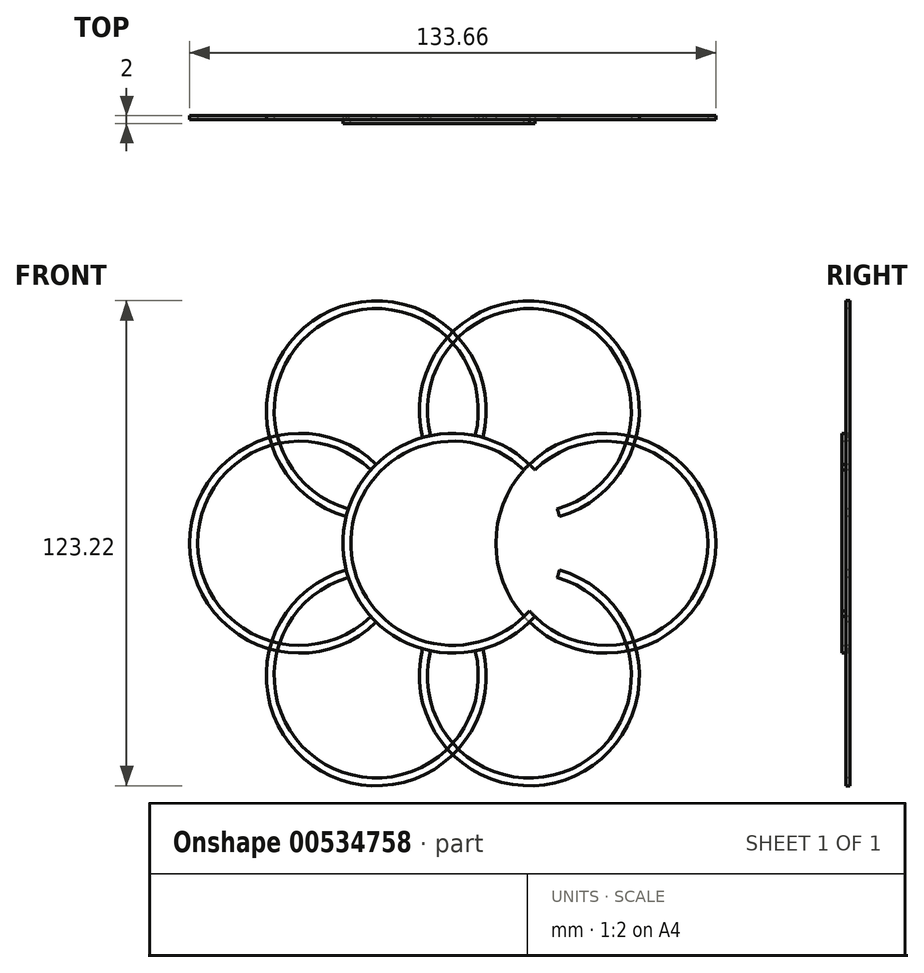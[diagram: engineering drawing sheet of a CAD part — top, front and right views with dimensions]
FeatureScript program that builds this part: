
annotation { "Feature Type Name" : "Feature", "Feature Type Description" : "" }
export const myFeature = defineFeature(function(context is Context, id is Id, definition is map)
    precondition{}
    {
        {
            var Q0;
            Q0=qCreatedBy(makeId("Front.planeOp"),FACE);
            var sketch = newSketch(context, id + "F0", { "sketchPlane" : qUnion([Q0])});
            skCircle(sketch, "E0", {"center": v(0, 0) * mm, "radius": 25.93 * mm});
            skCircle(sketch, "E1", {"center": v(38.9, 0) * mm, "radius": 25.93 * mm});
            skLineSegment(sketch, "E2", {"start": v(0, 0) * mm, "end": v(38.9, 0) * mm, "construction": true});
            skCircle(sketch, "E3", {"center": v(0, 0) * mm, "radius": 27.93 * mm});
            skCircle(sketch, "E4", {"center": v(38.9, 0) * mm, "radius": 27.93 * mm});
            skLineSegment(sketch, "E5", {"start": v(0, 25.93) * mm, "end": v(0, 0) * mm, "construction": true});
            skLineSegment(sketch, "E6", {"start": v(0, 0) * mm, "end": v(0, -25.93) * mm, "construction": true});
            skLineSegment(sketch, "E7", {"start": v(0, 12.97) * mm, "end": v(-27.93, 12.97) * mm, "construction": true});
            skLineSegment(sketch, "E8", {"start": v(-27.93, 12.97) * mm, "end": v(-27.93, -25.93) * mm, "construction": true});
            skLineSegment(sketch, "E9", {"start": v(-27.93, -25.93) * mm, "end": v(0, -25.93) * mm, "construction": true});
            skSolve(sketch);
        }
        {
            var Q0;
            {var subQ0=sQuery(id+"F0.wireOp",EDGE,"E4");var subQ1=sQuery(id+"F0.wireOp",EDGE,"E0");var subQ2=makeQuery(id+"F0.imprint","INTERSECT",VERTEX,{"disambiguationData":[OD(0.0)],"derivedFrom":[subQ1,subQ0]});Q0=makeQuery(id+"F0.imprint","IMPRINT",FACE,{"disambiguationData":[TD([[makeQuery(id+"F0.imprint","IMPRINT",EDGE,{"disambiguationData":[TD([[subQ2,1.0]])],"derivedFrom":subQ1}),1.0]])]});}
            var Q1;
            {var subQ0=sQuery(id+"F0.wireOp",EDGE,"E4");var subQ1=sQuery(id+"F0.wireOp",EDGE,"E0");var subQ2=makeQuery(id+"F0.imprint","INTERSECT",VERTEX,{"disambiguationData":[OD(0.0)],"derivedFrom":[subQ1,subQ0]});Q1=makeQuery(id+"F0.imprint","IMPRINT",FACE,{"disambiguationData":[TD([[makeQuery(id+"F0.imprint","IMPRINT",EDGE,{"disambiguationData":[TD([[subQ2,1.0]])],"derivedFrom":subQ1}),-1.0]])]});}
            var Q2;
            {var subQ0=sQuery(id+"F0.wireOp",EDGE,"E3");var subQ1=sQuery(id+"F0.wireOp",EDGE,"E1");var subQ2=makeQuery(id+"F0.imprint","INTERSECT",VERTEX,{"disambiguationData":[OD(0.0)],"derivedFrom":[subQ1,subQ0]});Q2=makeQuery(id+"F0.imprint","IMPRINT",FACE,{"disambiguationData":[TD([[makeQuery(id+"F0.imprint","IMPRINT",EDGE,{"disambiguationData":[TD([[subQ2,1.0]])],"derivedFrom":subQ1}),-1.0]])]});}
            var Q3;
            {var subQ0=sQuery(id+"F0.wireOp",EDGE,"E4");var subQ1=sQuery(id+"F0.wireOp",EDGE,"E0");var subQ2=makeQuery(id+"F0.imprint","INTERSECT",VERTEX,{"disambiguationData":[OD(1.0)],"derivedFrom":[subQ1,subQ0]});Q3=makeQuery(id+"F0.imprint","IMPRINT",FACE,{"disambiguationData":[TD([[makeQuery(id+"F0.imprint","IMPRINT",EDGE,{"disambiguationData":[TD([[subQ2,-1.0]])],"derivedFrom":subQ1}),-1.0]])]});}
            extrude(context, id + "F1", {"entities" : qUnion([Q0, Q1, Q2, Q3]), "oppositeDirection" : true, "depth" : 1 * mm, "offsetDistance" : 25 * mm});
        }
        {
            var Q0;
            {var subQ0=sQuery(id+"F0.wireOp",EDGE,"E4");var subQ1=sQuery(id+"F0.wireOp",EDGE,"E0");var subQ2=makeQuery(id+"F0.imprint","INTERSECT",VERTEX,{"disambiguationData":[OD(0.0)],"derivedFrom":[subQ1,subQ0]});Q0=makeQuery(id+"F0.imprint","IMPRINT",FACE,{"disambiguationData":[TD([[makeQuery(id+"F0.imprint","IMPRINT",EDGE,{"disambiguationData":[TD([[subQ2,-1.0]])],"derivedFrom":subQ1}),-1.0]])]});}
            var Q1;
            {var subQ0=sQuery(id+"F0.wireOp",EDGE,"E4");var subQ1=sQuery(id+"F0.wireOp",EDGE,"E0");var subQ2=makeQuery(id+"F0.imprint","INTERSECT",VERTEX,{"disambiguationData":[OD(0.0)],"derivedFrom":[subQ1,subQ0]});Q1=makeQuery(id+"F0.imprint","IMPRINT",FACE,{"disambiguationData":[TD([[makeQuery(id+"F0.imprint","IMPRINT",EDGE,{"disambiguationData":[TD([[subQ2,1.0]])],"derivedFrom":subQ1}),-1.0]])]});}
            var Q2;
            {var subQ0=sQuery(id+"F0.wireOp",EDGE,"E4");var subQ1=sQuery(id+"F0.wireOp",EDGE,"E0");var subQ2=makeQuery(id+"F0.imprint","INTERSECT",VERTEX,{"disambiguationData":[OD(1.0)],"derivedFrom":[subQ1,subQ0]});Q2=makeQuery(id+"F0.imprint","IMPRINT",FACE,{"disambiguationData":[TD([[makeQuery(id+"F0.imprint","IMPRINT",EDGE,{"disambiguationData":[TD([[subQ2,-1.0]])],"derivedFrom":subQ1}),-1.0]])]});}
            var Q3;
            {var subQ0=sQuery(id+"F0.wireOp",EDGE,"E1");var subQ1=sQuery(id+"F0.wireOp",EDGE,"E0");var subQ2=makeQuery(id+"F0.imprint","INTERSECT",VERTEX,{"disambiguationData":[OD(0.0)],"derivedFrom":[subQ1,subQ0]});Q3=makeQuery(id+"F0.imprint","IMPRINT",FACE,{"disambiguationData":[TD([[makeQuery(id+"F0.imprint","IMPRINT",EDGE,{"disambiguationData":[TD([[subQ2,1.0]])],"derivedFrom":subQ1}),-1.0]])]});}
            extrude(context, id + "F2", {"entities" : qUnion([Q0, Q1, Q2, Q3]), "depth" : 1 * mm, "offsetDistance" : 25 * mm});
        }
        {
            var Q0;
            Q0=qCreatedBy(makeId("Top.planeOp"),FACE);
            var sketch = newSketch(context, id + "F3", { "sketchPlane" : qUnion([Q0])});
            skLineSegment(sketch, "E10", {"start": v(0, 19) * mm, "end": v(0, -28.53) * mm});
            skSolve(sketch);
        }
        {
            var Q0;
            Q0=makeQuery(id+"F1.opExtrude","SWEPT_BODY",BODY,{"disambiguationData":[OSD([sQuery(id+"F0.wireOp",EDGE,"E1"),sQuery(id+"F0.wireOp",EDGE,"E4")])]});
            var Q1;
            Q1=sQuery(id+"F3.wireOp",EDGE,"E10");
            circularPattern(context, id + "F4", {"entities" : qUnion([Q0]), "axis" : qUnion([Q1]), "angle" : 360 * degree, "instanceCount" : 6, "equalSpace" : true});
        }
    });
